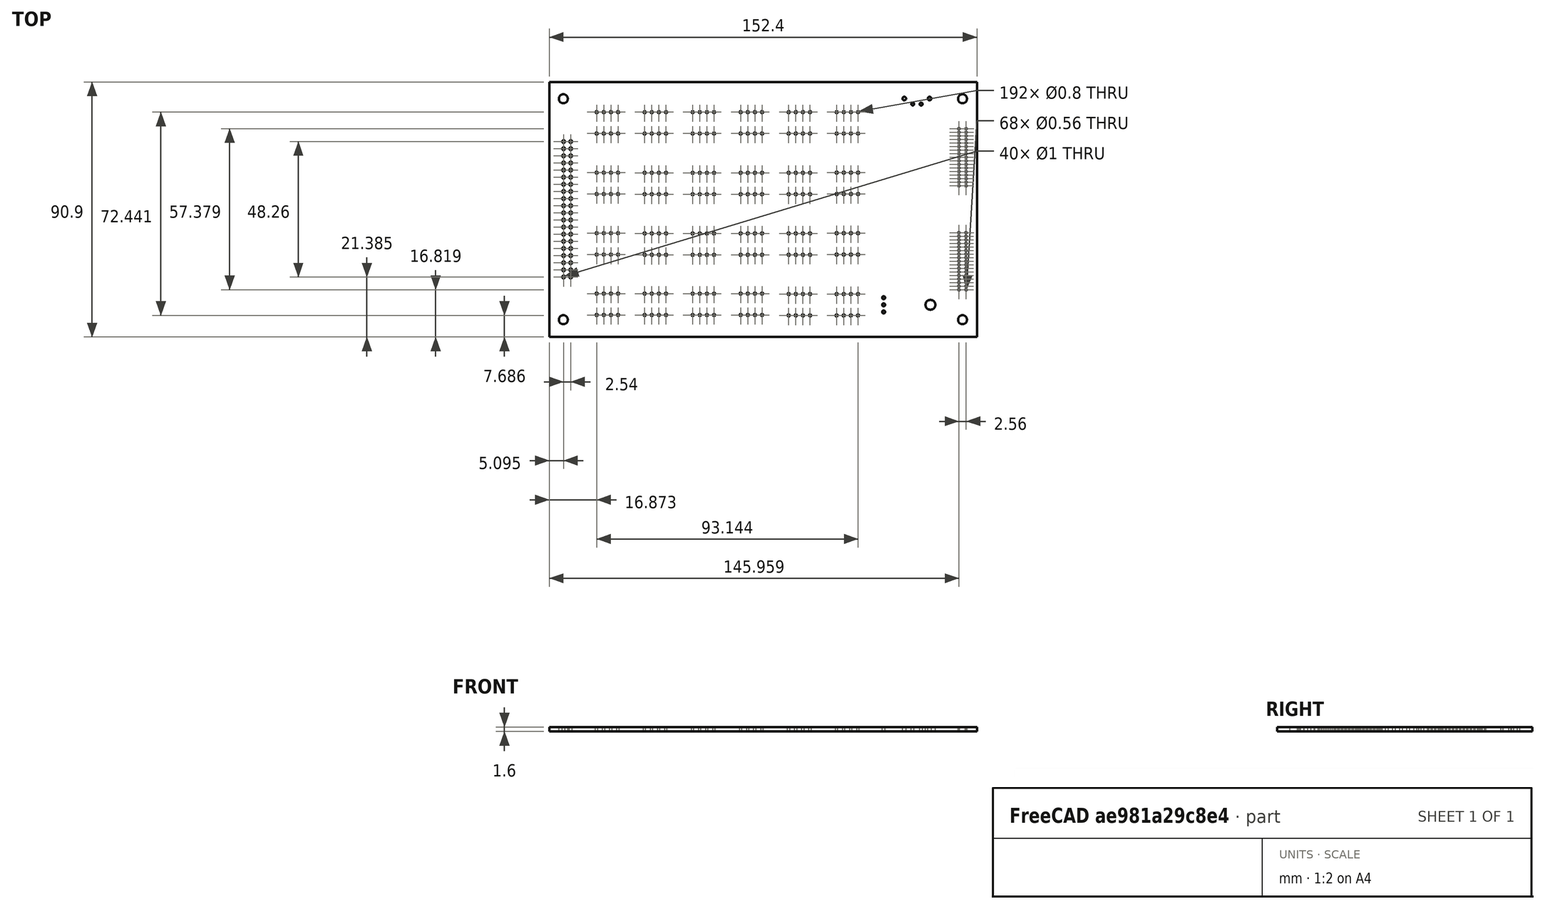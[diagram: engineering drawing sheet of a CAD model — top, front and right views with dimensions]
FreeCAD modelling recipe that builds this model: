
FCSTD DOCUMENT  (FreeCAD 0.20R29603 (Git))
Label: Op
License: All rights reserved
LicenseURL: http://en.wikipedia.org/wiki/All_rights_reserved
objects: Sketcher::SketchObject×2, Part::Feature×1, App::Part×1, PartDesign::ShapeBinder×1, PartDesign::Body×1
note: 5 computed .brp shape members not serialized (recipe doc carries the construction recipe); baked Part::Feature solids carry a one-line shape summary decoded from their .brp

FEATURE [Part::Feature] Part__Feature  label="DCT_Opamp_heater_board PCB"
  shape: bbox 152.4 x 90.9 x 1.6 mm, 318 faces (baked)
FEATURE [App::Part] DCT_Opamp_heater_board_1  label="DCT_Opamp_heater_board 1"
  Group = -> [Part__Feature]
  Origin = -> Origin
FEATURE [PartDesign::ShapeBinder] ShapeBinder
  Support = -> [Part__Feature]
  TraceSupport = false
FEATURE [Sketcher::SketchObject] Sketch
  ExternalGeometry = -> [ShapeBinder]
  FullyConstrained = true
  MapMode = 5
  Placement = pos=(0,0,1.6) rot=(0,0,1;0rad)
  Support = -> [ShapeBinder]
FEATURE [Sketcher::SketchObject] Sketch001
  FullyConstrained = true
  MapMode = 5
  Placement = pos=(0,0,1.6) rot=(0,0,1;0rad)
  Support = -> [ShapeBinder]
FEATURE [PartDesign::Body] Body
  Group = -> [ShapeBinder,Sketch,Sketch001]
  Origin = -> Origin001
